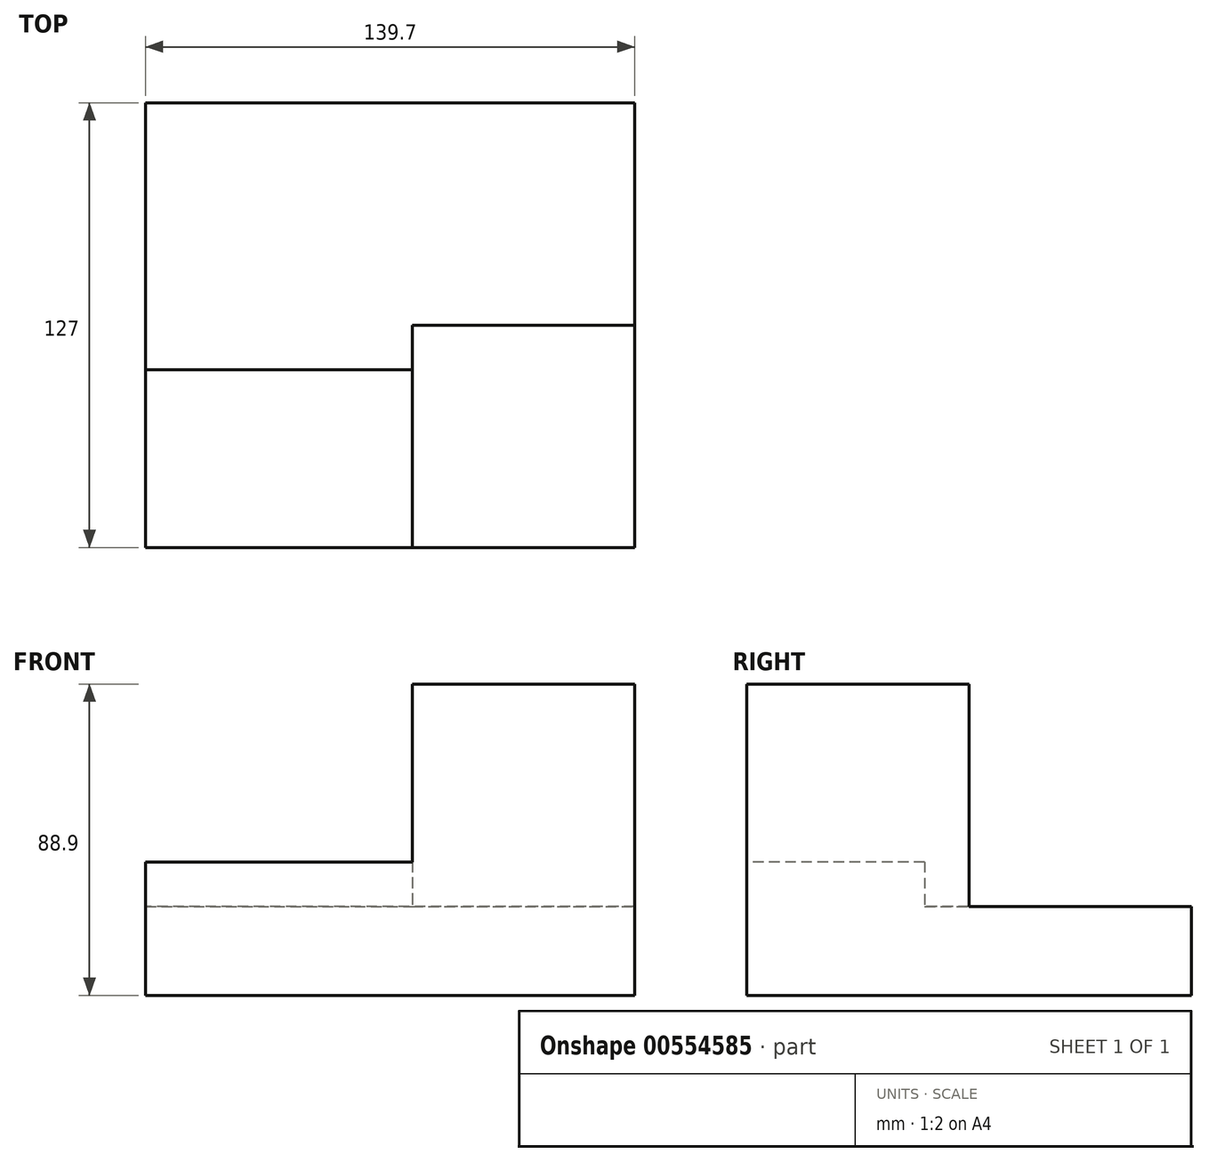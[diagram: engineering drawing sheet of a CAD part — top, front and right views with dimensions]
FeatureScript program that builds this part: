
annotation { "Feature Type Name" : "Feature", "Feature Type Description" : "" }
export const myFeature = defineFeature(function(context is Context, id is Id, definition is map)
    precondition{}
    {
        {
            var Q0;
            Q0=qCreatedBy(makeId("Top.planeOp"),FACE);
            var sketch = newSketch(context, id + "F0", { "sketchPlane" : qUnion([Q0])});
            skLineSegment(sketch, "E0.bottom", {"start": v(63.5, -63.5) * mm, "end": v(-76.2, -63.5) * mm});
            skLineSegment(sketch, "E0.top", {"start": v(63.5, 63.5) * mm, "end": v(-76.2, 63.5) * mm});
            skLineSegment(sketch, "E0.left", {"start": v(63.5, -63.5) * mm, "end": v(63.5, 63.5) * mm});
            skLineSegment(sketch, "E0.right", {"start": v(-76.2, -63.5) * mm, "end": v(-76.2, 63.5) * mm});
            skLineSegment(sketch, "E1.bottom", {"start": v(0, 0) * mm, "end": v(63.5, 0) * mm});
            skLineSegment(sketch, "E1.top", {"start": v(0, -63.5) * mm, "end": v(63.5, -63.5) * mm});
            skLineSegment(sketch, "E1.left", {"start": v(0, 0) * mm, "end": v(0, -63.5) * mm});
            skLineSegment(sketch, "E1.right", {"start": v(63.5, 0) * mm, "end": v(63.5, -63.5) * mm});
            skLineSegment(sketch, "E2.bottom", {"start": v(-76.2, -12.7) * mm, "end": v(0, -12.7) * mm});
            skLineSegment(sketch, "E2.top", {"start": v(-76.2, -63.5) * mm, "end": v(0, -63.5) * mm});
            skLineSegment(sketch, "E2.left", {"start": v(-76.2, -12.7) * mm, "end": v(-76.2, -63.5) * mm});
            skLineSegment(sketch, "E2.right", {"start": v(0, -12.7) * mm, "end": v(0, -63.5) * mm});
            skSolve(sketch);
        }
        {
            var Q0;
            Q0=makeQuery(id+"F0.imprint","IMPRINT",FACE,{"disambiguationData":[TD([[makeQuery(id+"F0.imprint","IMPRINT",EDGE,{"derivedFrom":sQuery(id+"F0.wireOp",EDGE,"E1.bottom")}),-1.0]])]});
            extrude(context, id + "F1", {"entities" : qUnion([Q0]), "depth" : 88.9 * mm, "offsetDistance" : 25.4 * mm});
        }
        {
            var Q0;
            Q0=makeQuery(id+"F0.imprint","IMPRINT",FACE,{"disambiguationData":[TD([[makeQuery(id+"F0.imprint","IMPRINT",EDGE,{"derivedFrom":sQuery(id+"F0.wireOp",EDGE,"E2.bottom")}),-1.0]])]});
            extrude(context, id + "F2", {"entities" : qUnion([Q0]), "operationType" : NewBodyOperationType.ADD, "depth" : 38.1 * mm, "offsetDistance" : 25.4 * mm});
        }
        {
            var Q0;
            Q0=makeQuery(id+"F0.imprint","IMPRINT",FACE,{"disambiguationData":[TD([[makeQuery(id+"F0.imprint","IMPRINT",EDGE,{"derivedFrom":sQuery(id+"F0.wireOp",EDGE,"E0.top")}),1.0]])]});
            extrude(context, id + "F3", {"entities" : qUnion([Q0]), "operationType" : NewBodyOperationType.ADD, "depth" : 25.4 * mm, "offsetDistance" : 25.4 * mm});
        }
    });
